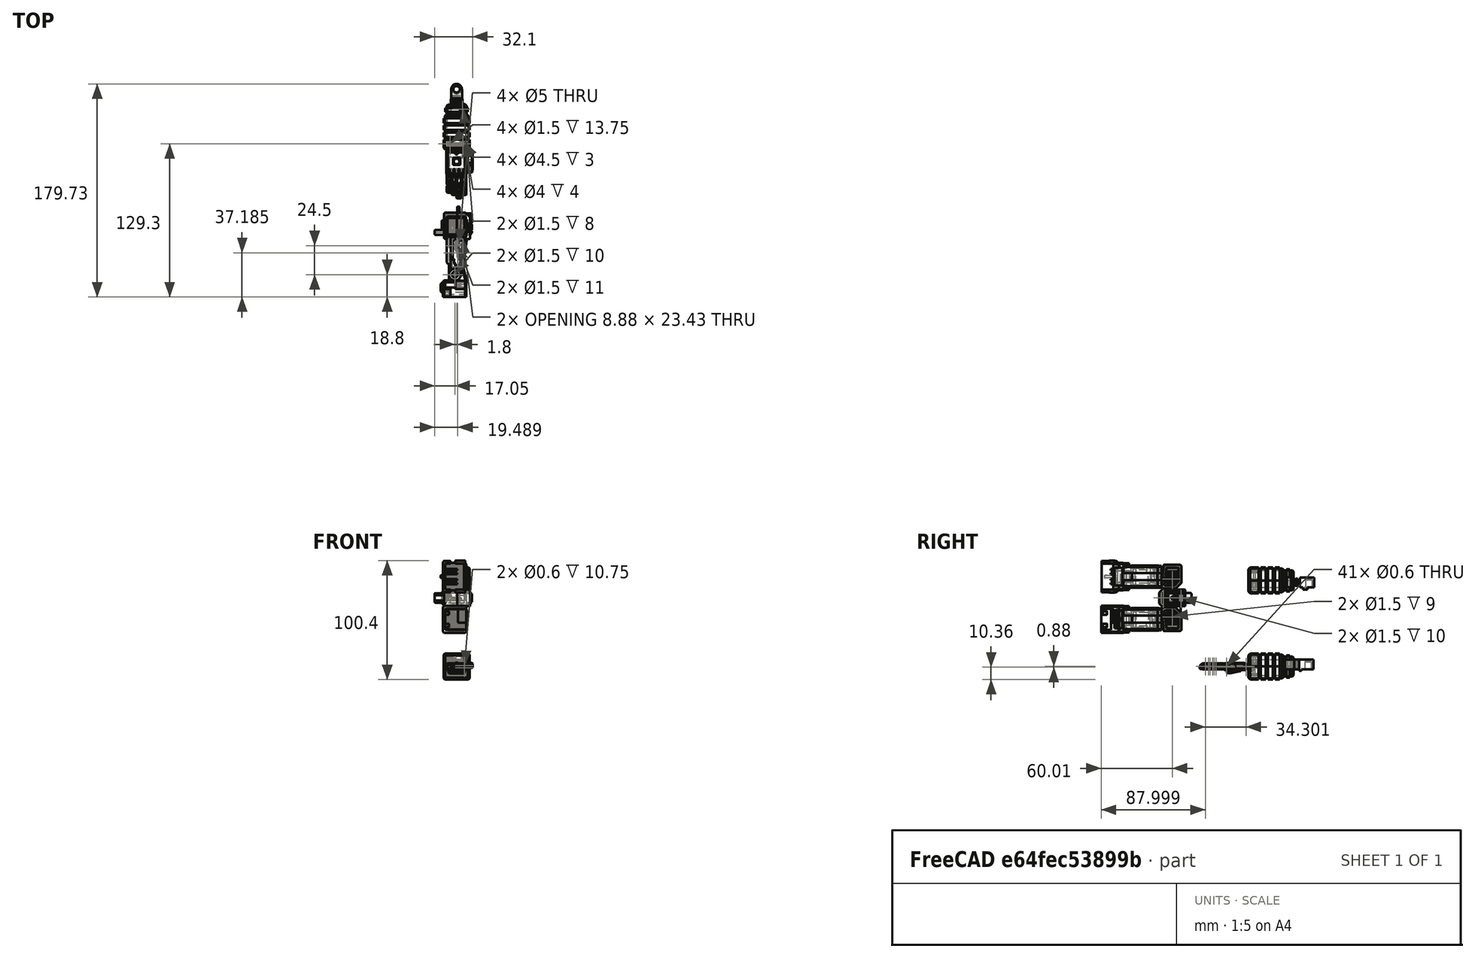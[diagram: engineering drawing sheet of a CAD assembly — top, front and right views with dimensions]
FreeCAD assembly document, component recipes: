
FREECAD ASSEMBLY — COMPONENT RECIPES ("Upgrades2")

This assembly document has 3 components, labeled P0..P2 below (a component is one placed body or linked part). 1 of them carries a construction recipe — the FreeCAD feature program that regenerates the part from scratch, quoted from this document or its linked companion documents; the rest are supplied as boundary geometry only. No exploded tour is included for this assembly.
COMPONENT P0 — geometry summary ("Left_Arm"; its construction recipe is too large to include in this document):
  bounding box: 96.1 x 24.5 x 21.9 mm
  tessellated surface: 52,052 triangles
  volume: 14380 mm^3 (28% of its bounding box)
COMPONENT P1 — recipe-attached ("Right_Arm", modeled in this document).
Construction recipe (the document's own serialized feature program — sketch geometry with constraints, then the solid features built on it; lengths are millimeters unless a unit is written):

FEATURE [Sketcher::SketchObject] Sketch980
  ArcFitTolerance = 1e-06
  AttachmentSupport = -> [XY_Plane090]
  FullyConstrained = true
  MakeInternals = false
  MapMode = 5
  sketch-geometry (2):
    g0: Circle CenterX=0 CenterY=0 CenterZ=0 NormalX=0 NormalY=0 NormalZ=1 AngleXU=0 Radius=2.725
    g1: Circle CenterX=0 CenterY=0 CenterZ=0 NormalX=0 NormalY=0 NormalZ=1 AngleXU=0 Radius=4.5
  constraints (4):
    c: Coincident(g0,g-1)
    c: Coincident(g1,g0)
    c: Radius(g0) = 2.725
    c: Radius(g1) = 4.5
FEATURE [PartDesign::Pad] Pad633
  Direction = (0,0,1)
  Length = 8.2
  Length2 = 10
  Profile = -> Sketch980
  ReferenceAxis = -> Sketch980 [N_Axis]
  Refine = true
  Suppressed = false
  Type = 0
FEATURE [Sketcher::SketchObject] Sketch981
  ArcFitTolerance = 1e-06
  AttachmentSupport = -> [Pad633]
  ExternalGeometry = -> [Pad633]
  FullyConstrained = true
  MakeInternals = false
  MapMode = 5
  Placement = pos=(0,0,8.2) rot=(0,0,1;0rad)
  sketch-geometry (6):
    g0: LineSegment StartX=-4.5 StartY=-3e-16 StartZ=0 EndX=-4.5 EndY=-7.5 EndZ=0
    g1: LineSegment StartX=-4.5 StartY=-7.5 StartZ=0 EndX=4.5 EndY=-7.5 EndZ=0
    g2: LineSegment StartX=4.5 StartY=0 StartZ=0 EndX=4.5 EndY=-7.5 EndZ=0
    g3: LineSegment [constr] StartX=0 StartY=4.5 StartZ=0 EndX=-4.5 EndY=4.5 EndZ=0
    g4: LineSegment [constr] StartX=-4.5 StartY=4.5 StartZ=0 EndX=-4.5 EndY=0 EndZ=0
    g5: ArcOfCircle CenterX=-1e-16 CenterY=-7.65348e-06 CenterZ=0 NormalX=0 NormalY=0 NormalZ=1 AngleXU=0 Radius=4.5 StartAngle=3.14159 EndAngle=6.28319
  constraints (19):
    c: PointOnObject(g0,g-3)
    c: Vertical(g0)
    c: Coincident(g1,g0)
    c: Horizontal(g1)
    c: PointOnObject(g2,g-3)
    c: Coincident(g2,g1)
    c: Vertical(g2)
    c: PointOnObject(g3,g-3)
    c: Coincident(g4,g3)
    c: Coincident(g4,g0)
    c: Vertical(g4)
    c: Horizontal(g3)
    c: DistanceY(g0,g3) = 12
    c: PointOnObject(g2,g-1)
    c: PointOnObject(g0,g-1)
    c: PointOnObject(g3,g-2)
    c: Coincident(g5,g0)
    c: Coincident(g5,g2)
    c: Tangent(g5,g-3)
FEATURE [PartDesign::Pad] Pad634
  BaseFeature = -> Pad633
  Direction = (0,0,1)
  Length = 8.2
  Length2 = 10
  Profile = -> Sketch981
  ReferenceAxis = -> Sketch981 [N_Axis]
  Refine = true
  Reversed = true
  Suppressed = false
  Type = 0
FEATURE [Sketcher::SketchObject] Sketch982
  ArcFitTolerance = 1e-06
  AttachmentSupport = -> [Pad634]
  ExternalGeometry = -> [Pad634]
  FullyConstrained = true
  MakeInternals = false
  MapMode = 5
  Placement = pos=(0,-7.5,0) rot=(1,0,0;1.5708rad)
  sketch-geometry (1):
    g0: Circle CenterX=0 CenterY=4.1 CenterZ=0 NormalX=0 NormalY=0 NormalZ=1 AngleXU=0 Radius=2
  constraints (4):
    c: PointOnObject(g0,g-2)
    c: DistanceY(g-4,g-4) = 8.2
    c: DistanceY(g0,g-4) = 4.1
    c: Radius(g0) = 2
FEATURE [PartDesign::Pad] Pad635
  BaseFeature = -> Pad634
  Direction = (0,-1,2e-16)
  Length = 2
  Length2 = 10
  Profile = -> Sketch982
  ReferenceAxis = -> Sketch982 [N_Axis]
  Refine = true
  Suppressed = false
  Type = 0
FEATURE [Sketcher::SketchObject] Sketch983
  ArcFitTolerance = 1e-06
  AttachmentSupport = -> [Pad635]
  ExternalGeometry = -> [Pad635]
  FullyConstrained = true
  MakeInternals = false
  MapMode = 5
  Placement = pos=(0,-9.5,0) rot=(1,0,0;1.5708rad)
  sketch-geometry (1):
    g0: Circle CenterX=0 CenterY=4.1 CenterZ=0 NormalX=0 NormalY=0 NormalZ=1 AngleXU=0 Radius=3
  constraints (2):
    c: Coincident(g0,g-3)
    c: Radius(g0) = 3
FEATURE [PartDesign::Pad] Pad636
  BaseFeature = -> Pad635
  Direction = (0,-1,2e-16)
  Length = 2
  Length2 = 10
  Profile = -> Sketch983
  ReferenceAxis = -> Sketch983 [N_Axis]
  Refine = true
  Suppressed = false
  Type = 0
FEATURE [Sketcher::SketchObject] Sketch984
  ArcFitTolerance = 1e-06
  AttachmentOffset = pos=(0,0,-1) rot=(0,0,1;0rad)
  AttachmentSupport = -> [Pad636]
  ExternalGeometry = -> [Pad636]
  FullyConstrained = false
  MakeInternals = false
  MapMode = 5
  Placement = pos=(0,0,7.2) rot=(0,0,1;0rad)
  sketch-geometry (1):
    g0: Circle CenterX=0 CenterY=0 CenterZ=0 NormalX=0 NormalY=0 NormalZ=1 AngleXU=0 Radius=2.75
  constraints (1):
    c: Coincident(g0,g-1)
FEATURE [PartDesign::Pad] Pad637
  BaseFeature = -> Pad636
  Direction = (0,0,1)
  Length = 0.9
  Length2 = 10
  Profile = -> Sketch984
  ReferenceAxis = -> Sketch984 [N_Axis]
  Refine = true
  Reversed = true
  Suppressed = false
  Type = 0
FEATURE [PartDesign::Pad] Pad638
  BaseFeature = -> Pad637
  Direction = (0,-1,3e-16)
  Length = 0.1
  Length2 = 10
  Profile = -> Pad637 [Face14]
  Refine = true
  Suppressed = false
  Type = 0
FEATURE [PartDesign::Chamfer] Chamfer060
  Angle = 45
  Base = -> Pad638 [Edge1]
  BaseFeature = -> Pad638
  ChamferType = 0
  FlipDirection = false
  Refine = true
  Size = 0.5
  Size2 = 1
  SupportTransform = false
  Suppressed = false
  UseAllEdges = false
FEATURE [Sketcher::SketchObject] Sketch985
  ArcFitTolerance = 1e-06
  AttachmentSupport = -> [Chamfer060]
  ExternalGeometry = -> [Chamfer060]
  FullyConstrained = true
  MakeInternals = false
  MapMode = 5
  Placement = pos=(0,0,0) rot=(1,0,0;3.14159rad)
  sketch-geometry (6):
    g0: LineSegment StartX=-4.5 StartY=1 StartZ=0 EndX=-4.5 EndY=5 EndZ=0
    g1: LineSegment StartX=-4.5 StartY=5 StartZ=0 EndX=4.5 EndY=5 EndZ=0
    g2: LineSegment StartX=4.5 StartY=5 StartZ=0 EndX=4.5 EndY=1 EndZ=0
    g3: LineSegment StartX=4.5 StartY=1 StartZ=0 EndX=3.1 EndY=2.4 EndZ=0
    g4: LineSegment StartX=-4.5 StartY=1 StartZ=0 EndX=-3.1 EndY=2.4 EndZ=0
    g5: ArcOfCircle CenterX=5e-16 CenterY=-0.507318 CenterZ=0 NormalX=0 NormalY=0 NormalZ=1 AngleXU=0 Radius=4.25 StartAngle=0.753335 EndAngle=2.38826
  constraints (19):
    c: PointOnObject(g0,g-3)
    c: PointOnObject(g0,g-3)
    c: Coincident(g1,g0)
    c: PointOnObject(g1,g-5)
    c: Horizontal(g1)
    c: Coincident(g2,g1)
    c: PointOnObject(g2,g-5)
    c: Coincident(g3,g2)
    c: Coincident(g4,g0)
    c: DistanceY(g0,g0) = 4
    c: DistanceY(g3,g4) = 0
    c: DistanceY(g2,g2) = 4
    c: DistanceY(g0,g-4) = 2.5
    c: Angle(g4,g0) = 0.785398
    c: Coincident(g5,g4)
    c: Coincident(g5,g3)
    c: Angle(g2,g3) = 0.785398
    c: Radius(g5) = 4.25
    c: DistanceY(g-1,g4) = 2.4
FEATURE [PartDesign::Pad] Pad639
  BaseFeature = -> Chamfer060
  Direction = (0,0,-1)
  Length = 2
  Length2 = 10
  Profile = -> Sketch985
  ReferenceAxis = -> Sketch985 [N_Axis]
  Refine = true
  Suppressed = false
  Type = 0
FEATURE [PartDesign::Body] Body080  label="Right_Connector"
  AllowCompound = false
  Group = -> [Sketch980,Pad633,Sketch981,Pad634,Sketch982,Pad635,Sketch983,Pad636,Sketch984,Pad637,Pad638,Chamfer060,Sketch985,Pad639]
  Origin = -> Origin090
  Placement = pos=(0,0.63,67.1) rot=(0,0,1;0rad)
  Tip = -> Pad639
COMPONENT P2 — geometry summary ("Waist"; its construction recipe is too large to include in this document):
  bounding box: 76.2 x 61.1 x 31.5 mm
  tessellated surface: 103,156 triangles
  volume: 32345 mm^3 (22% of its bounding box)
PROVENANCE & LICENSES
A FreeCAD (.FCStd) document from a public repository crawl; recipes are the document's own serialized feature recipes (and, for linked parts, companion documents' recipes).
License: as declared in the source repository (recorded in the dataset sidecar).
